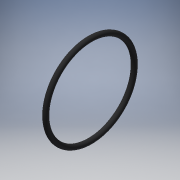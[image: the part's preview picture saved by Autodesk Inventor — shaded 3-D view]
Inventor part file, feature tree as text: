
AUTODESK INVENTOR PART (.ipt)
format: ipt  version: 2019.4 (Build 234330000, 330)  size: 160,256 bytes
history: native  units: in
note: dims shown in document units (in); Inventor stores cm internally (conversion verified against a paired STEP export)
features: sketch x2, sweep x1
ambient origin geometry x8: Origin, YZ Plane, XZ Plane, XY Plane, X Axis, Y Axis, Z Axis, Center Point
bodies: Solid1 (feature_tree)
feature tree (3):
  sweep  "Sweep1"
  sketch  "Sketch1"  dims[d0=0.103in d1=1.737in]
  sketch  "Sketch2"  dims[d2=1.943in d3=0.0in d4=0.0in]
